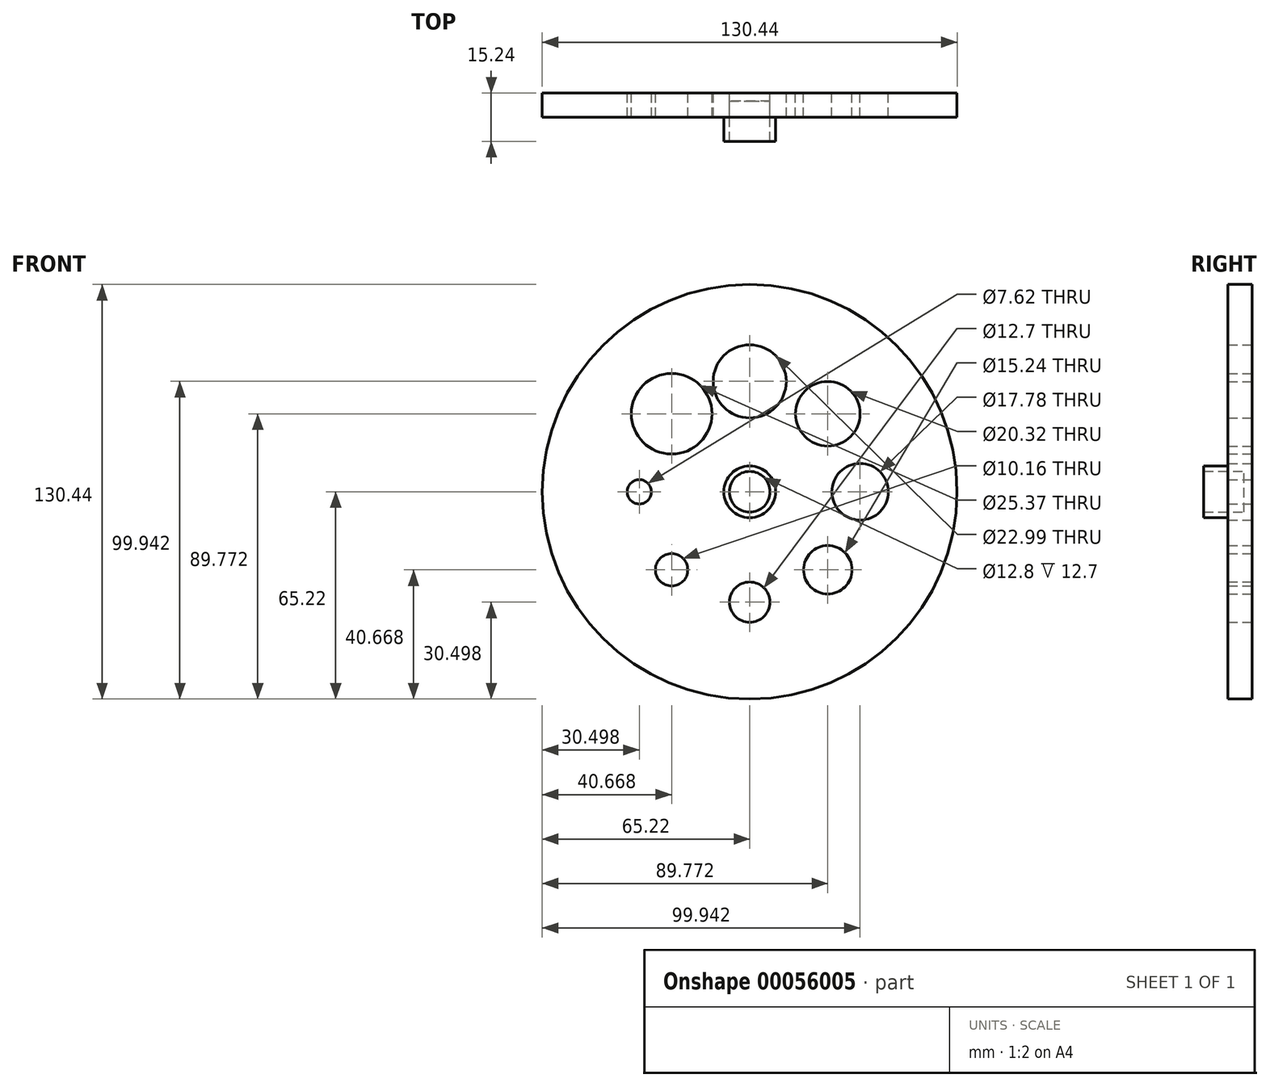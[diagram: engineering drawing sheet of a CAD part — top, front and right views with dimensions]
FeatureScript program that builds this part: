
annotation { "Feature Type Name" : "Feature", "Feature Type Description" : "" }
export const myFeature = defineFeature(function(context is Context, id is Id, definition is map)
    precondition{}
    {
        {
            var Q0;
            Q0=qCreatedBy(makeId("Front.planeOp"),FACE);
            var sketch = newSketch(context, id + "F0", { "sketchPlane" : qUnion([Q0])});
            skCircle(sketch, "E0", {"center": v(0, 34.72) * mm, "radius": 11.5 * mm});
            skCircle(sketch, "E1", {"center": v(-24.55, 24.55) * mm, "radius": 12.69 * mm});
            skCircle(sketch, "E2", {"center": v(-24.55, -24.55) * mm, "radius": 5.08 * mm});
            skCircle(sketch, "E3", {"center": v(0, 34.72) * mm, "radius": 11.43 * mm});
            skCircle(sketch, "E4", {"center": v(24.55, 24.55) * mm, "radius": 10.16 * mm});
            skCircle(sketch, "E5", {"center": v(34.72, 0) * mm, "radius": 8.9 * mm});
            skCircle(sketch, "E6", {"center": v(24.55, -24.55) * mm, "radius": 7.62 * mm});
            skCircle(sketch, "E7", {"center": v(0, -34.72) * mm, "radius": 6.35 * mm});
            skCircle(sketch, "E8", {"center": v(-34.72, 0) * mm, "radius": 3.81 * mm});
            skCircle(sketch, "E9", {"center": v(0, 0) * mm, "radius": 65.22 * mm});
            skSolve(sketch);
        }
        {
            var Q0;
            Q0=makeQuery(id+"F0.imprint","IMPRINT",FACE,{"disambiguationData":[TD([[makeQuery(id+"F0.imprint","IMPRINT",EDGE,{"derivedFrom":sQuery(id+"F0.wireOp",EDGE,"E0")}),-1.0]])]});
            extrude(context, id + "F1", {"entities" : qUnion([Q0]), "depth" : 7.62 * mm});
        }
        {
            var Q0;
            Q0=qCreatedBy(makeId("Front.planeOp"),FACE);
            var sketch = newSketch(context, id + "F2", { "sketchPlane" : qUnion([Q0])});
            skCircle(sketch, "E10", {"center": v(0, 0) * mm, "radius": 8.14 * mm});
            skCircle(sketch, "E11", {"center": v(0, 0) * mm, "radius": 6.4 * mm});
            skSolve(sketch);
        }
        {
            var Q0;
            Q0 = qSketchRegion(id + "F2", true);
            extrude(context, id + "F3", {"entities" : qUnion([Q0]), "operationType" : NewBodyOperationType.ADD, "depth" : 15.24 * mm});
        }
        {
            var Q0;
            Q0=makeQuery(id+"F3.boolean.opBoolean","SPLIT",FACE,{"disambiguationData":[TD([makeQuery(id+"F3.opExtrude","SWEPT_FACE",FACE,{"disambiguationData":[OSD([sQuery(id+"F2.wireOp",EDGE,"E11")])]})])],"derivedFrom":makeQuery(id+"F1.opExtrude","CAP_FACE",FACE,{"disambiguationData":[OSD([sQuery(id+"F0.wireOp",EDGE,"E0"),sQuery(id+"F0.wireOp",EDGE,"E2"),sQuery(id+"F0.wireOp",EDGE,"E4"),sQuery(id+"F0.wireOp",EDGE,"E5"),sQuery(id+"F0.wireOp",EDGE,"E6"),sQuery(id+"F0.wireOp",EDGE,"E7"),sQuery(id+"F0.wireOp",EDGE,"E8"),sQuery(id+"F0.wireOp",EDGE,"E1"),sQuery(id+"F0.wireOp",EDGE,"E9")])],"isStart":false})});
            extrude(context, id + "F4", {"entities" : qUnion([Q0]), "operationType" : NewBodyOperationType.REMOVE, "oppositeDirection" : true, "depth" : 5.08 * mm});
        }
    });
